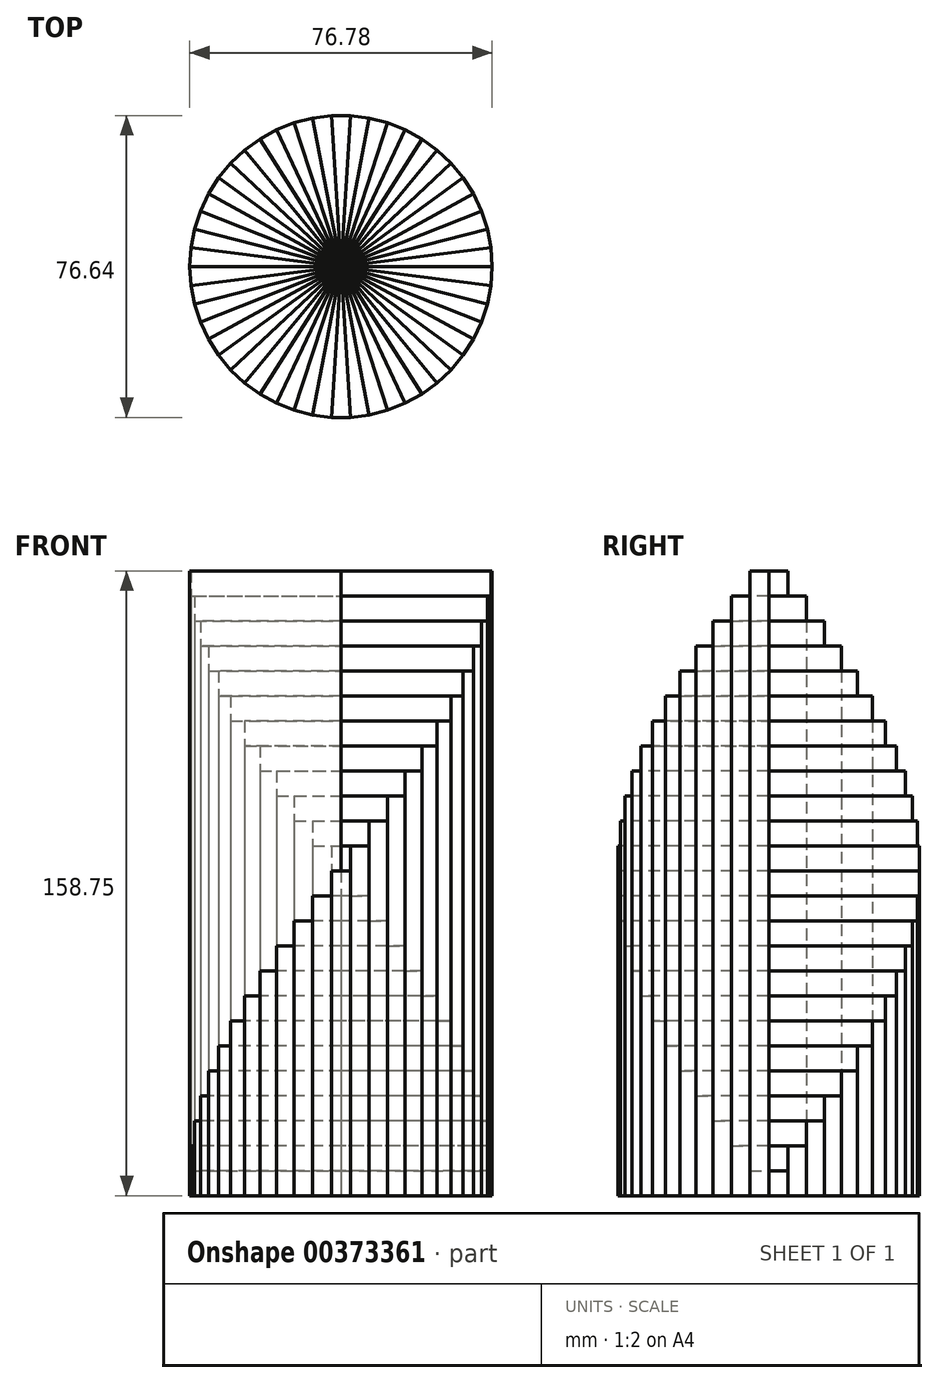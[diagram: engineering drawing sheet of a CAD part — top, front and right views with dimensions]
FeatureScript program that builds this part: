
annotation { "Feature Type Name" : "Feature", "Feature Type Description" : "" }
export const myFeature = defineFeature(function(context is Context, id is Id, definition is map)
    precondition{}
    {
        {
            var Q0;
            Q0=qCreatedBy(makeId("Top.planeOp"),FACE);
            var sketch = newSketch(context, id + "F0", { "sketchPlane" : qUnion([Q0])});
            skCircle(sketch, "E0.cCircle", {"center": v(0, 0) * mm, "radius": 38.32 * mm, "construction": true});
            skLineSegment(sketch, "E0.0", {"start": v(-2.41, 38.32) * mm, "end": v(2.41, 38.32) * mm});
            skLineSegment(sketch, "E0.1", {"start": v(2.41, 38.32) * mm, "end": v(7.2, 37.71) * mm});
            skLineSegment(sketch, "E0.2", {"start": v(7.2, 37.71) * mm, "end": v(11.86, 36.52) * mm});
            skLineSegment(sketch, "E0.3", {"start": v(11.86, 36.52) * mm, "end": v(16.35, 34.74) * mm});
            skLineSegment(sketch, "E0.4", {"start": v(16.35, 34.74) * mm, "end": v(20.57, 32.42) * mm});
            skLineSegment(sketch, "E0.5", {"start": v(20.57, 32.42) * mm, "end": v(24.47, 29.58) * mm});
            skLineSegment(sketch, "E0.6", {"start": v(24.47, 29.58) * mm, "end": v(27.99, 26.28) * mm});
            skLineSegment(sketch, "E0.7", {"start": v(27.99, 26.28) * mm, "end": v(31.06, 22.57) * mm});
            skLineSegment(sketch, "E0.8", {"start": v(31.06, 22.57) * mm, "end": v(33.65, 18.5) * mm});
            skLineSegment(sketch, "E0.9", {"start": v(33.65, 18.5) * mm, "end": v(35.7, 14.13) * mm});
            skLineSegment(sketch, "E0.10", {"start": v(35.7, 14.13) * mm, "end": v(37.19, 9.55) * mm});
            skLineSegment(sketch, "E0.11", {"start": v(37.19, 9.55) * mm, "end": v(38.1, 4.81) * mm});
            skLineSegment(sketch, "E0.12", {"start": v(38.1, 4.81) * mm, "end": v(38.4, 0) * mm});
            skLineSegment(sketch, "E0.13", {"start": v(38.4, 0) * mm, "end": v(38.1, -4.81) * mm});
            skLineSegment(sketch, "E0.14", {"start": v(38.1, -4.81) * mm, "end": v(37.19, -9.55) * mm});
            skLineSegment(sketch, "E0.15", {"start": v(37.19, -9.55) * mm, "end": v(35.7, -14.13) * mm});
            skLineSegment(sketch, "E0.16", {"start": v(35.7, -14.13) * mm, "end": v(33.65, -18.5) * mm});
            skLineSegment(sketch, "E0.17", {"start": v(33.65, -18.5) * mm, "end": v(31.06, -22.57) * mm});
            skLineSegment(sketch, "E0.18", {"start": v(31.06, -22.57) * mm, "end": v(27.99, -26.28) * mm});
            skLineSegment(sketch, "E0.19", {"start": v(27.99, -26.28) * mm, "end": v(24.47, -29.58) * mm});
            skLineSegment(sketch, "E0.20", {"start": v(24.47, -29.58) * mm, "end": v(20.57, -32.42) * mm});
            skLineSegment(sketch, "E0.21", {"start": v(20.57, -32.42) * mm, "end": v(16.35, -34.74) * mm});
            skLineSegment(sketch, "E0.22", {"start": v(16.35, -34.74) * mm, "end": v(11.86, -36.52) * mm});
            skLineSegment(sketch, "E0.23", {"start": v(11.86, -36.52) * mm, "end": v(7.2, -37.71) * mm});
            skLineSegment(sketch, "E0.24", {"start": v(7.2, -37.71) * mm, "end": v(2.41, -38.32) * mm});
            skLineSegment(sketch, "E0.25", {"start": v(2.41, -38.32) * mm, "end": v(-2.41, -38.32) * mm});
            skLineSegment(sketch, "E0.26", {"start": v(-2.41, -38.32) * mm, "end": v(-7.2, -37.71) * mm});
            skLineSegment(sketch, "E0.27", {"start": v(-7.2, -37.71) * mm, "end": v(-11.86, -36.52) * mm});
            skLineSegment(sketch, "E0.28", {"start": v(-11.86, -36.52) * mm, "end": v(-16.35, -34.74) * mm});
            skLineSegment(sketch, "E0.29", {"start": v(-16.35, -34.74) * mm, "end": v(-20.57, -32.42) * mm});
            skLineSegment(sketch, "E0.30", {"start": v(-20.57, -32.42) * mm, "end": v(-24.47, -29.58) * mm});
            skLineSegment(sketch, "E0.31", {"start": v(-24.47, -29.58) * mm, "end": v(-27.99, -26.28) * mm});
            skLineSegment(sketch, "E0.32", {"start": v(-27.99, -26.28) * mm, "end": v(-31.06, -22.57) * mm});
            skLineSegment(sketch, "E0.33", {"start": v(-31.06, -22.57) * mm, "end": v(-33.65, -18.5) * mm});
            skLineSegment(sketch, "E0.34", {"start": v(-33.65, -18.5) * mm, "end": v(-35.7, -14.13) * mm});
            skLineSegment(sketch, "E0.35", {"start": v(-35.7, -14.13) * mm, "end": v(-37.19, -9.55) * mm});
            skLineSegment(sketch, "E0.36", {"start": v(-37.19, -9.55) * mm, "end": v(-38.1, -4.81) * mm});
            skLineSegment(sketch, "E0.37", {"start": v(-38.1, -4.81) * mm, "end": v(-38.4, 0) * mm});
            skLineSegment(sketch, "E0.38", {"start": v(-38.4, 0) * mm, "end": v(-38.1, 4.81) * mm});
            skLineSegment(sketch, "E0.39", {"start": v(-38.1, 4.81) * mm, "end": v(-37.19, 9.55) * mm});
            skLineSegment(sketch, "E0.40", {"start": v(-37.19, 9.55) * mm, "end": v(-35.7, 14.13) * mm});
            skLineSegment(sketch, "E0.41", {"start": v(-35.7, 14.13) * mm, "end": v(-33.65, 18.5) * mm});
            skLineSegment(sketch, "E0.42", {"start": v(-33.65, 18.5) * mm, "end": v(-31.06, 22.57) * mm});
            skLineSegment(sketch, "E0.43", {"start": v(-31.06, 22.57) * mm, "end": v(-27.99, 26.28) * mm});
            skLineSegment(sketch, "E0.44", {"start": v(-27.99, 26.28) * mm, "end": v(-24.47, 29.58) * mm});
            skLineSegment(sketch, "E0.45", {"start": v(-24.47, 29.58) * mm, "end": v(-20.57, 32.42) * mm});
            skLineSegment(sketch, "E0.46", {"start": v(-20.57, 32.42) * mm, "end": v(-16.35, 34.74) * mm});
            skLineSegment(sketch, "E0.47", {"start": v(-16.35, 34.74) * mm, "end": v(-11.86, 36.52) * mm});
            skLineSegment(sketch, "E0.48", {"start": v(-11.86, 36.52) * mm, "end": v(-7.2, 37.71) * mm});
            skLineSegment(sketch, "E0.49", {"start": v(-7.2, 37.71) * mm, "end": v(-2.41, 38.32) * mm});
            skPoint(sketch, "E0.0.midPoint", {"position": v(0, 38.32) * mm});
            skLineSegment(sketch, "E1", {"start": v(-38.4, 0) * mm, "end": v(38.4, 0) * mm});
            skLineSegment(sketch, "E2", {"start": v(38.1, 4.81) * mm, "end": v(-38.1, -4.81) * mm});
            skLineSegment(sketch, "E3", {"start": v(37.19, 9.55) * mm, "end": v(-37.19, -9.55) * mm});
            skLineSegment(sketch, "E4", {"start": v(35.7, 14.13) * mm, "end": v(-35.7, -14.13) * mm});
            skLineSegment(sketch, "E5", {"start": v(33.65, 18.5) * mm, "end": v(-33.65, -18.5) * mm});
            skLineSegment(sketch, "E6", {"start": v(31.06, 22.57) * mm, "end": v(-31.06, -22.57) * mm});
            skLineSegment(sketch, "E7", {"start": v(27.99, 26.28) * mm, "end": v(-27.99, -26.28) * mm});
            skLineSegment(sketch, "E8", {"start": v(24.47, 29.58) * mm, "end": v(-24.47, -29.58) * mm});
            skLineSegment(sketch, "E9", {"start": v(20.57, 32.42) * mm, "end": v(-20.57, -32.42) * mm});
            skLineSegment(sketch, "E10", {"start": v(16.35, 34.74) * mm, "end": v(-16.35, -34.74) * mm});
            skLineSegment(sketch, "E11", {"start": v(11.86, 36.52) * mm, "end": v(-11.86, -36.52) * mm});
            skLineSegment(sketch, "E12", {"start": v(7.2, 37.71) * mm, "end": v(-7.2, -37.71) * mm});
            skLineSegment(sketch, "E13", {"start": v(2.41, 38.32) * mm, "end": v(-2.41, -38.32) * mm});
            skLineSegment(sketch, "E14", {"start": v(-2.41, 38.32) * mm, "end": v(2.41, -38.32) * mm});
            skLineSegment(sketch, "E15", {"start": v(-7.2, 37.71) * mm, "end": v(7.2, -37.71) * mm});
            skLineSegment(sketch, "E16", {"start": v(-11.86, 36.52) * mm, "end": v(11.86, -36.52) * mm});
            skLineSegment(sketch, "E17", {"start": v(-16.35, 34.74) * mm, "end": v(16.35, -34.74) * mm});
            skLineSegment(sketch, "E18", {"start": v(-20.57, 32.42) * mm, "end": v(20.57, -32.42) * mm});
            skLineSegment(sketch, "E19", {"start": v(24.47, -29.58) * mm, "end": v(-24.47, 29.58) * mm});
            skLineSegment(sketch, "E20", {"start": v(-27.99, 26.28) * mm, "end": v(27.99, -26.28) * mm});
            skLineSegment(sketch, "E21", {"start": v(31.06, -22.57) * mm, "end": v(-31.06, 22.57) * mm});
            skLineSegment(sketch, "E22", {"start": v(-33.65, 18.5) * mm, "end": v(33.65, -18.5) * mm});
            skLineSegment(sketch, "E23", {"start": v(35.7, -14.13) * mm, "end": v(-35.7, 14.13) * mm});
            skLineSegment(sketch, "E24", {"start": v(-37.19, 9.55) * mm, "end": v(37.19, -9.55) * mm});
            skLineSegment(sketch, "E25", {"start": v(-38.1, 4.81) * mm, "end": v(38.1, -4.81) * mm});
            skSolve(sketch);
        }
        {
            var Q0;
            {var subQ0=sQuery(id+"F0.wireOp",EDGE,"E0.12");Q0=makeQuery(id+"F0.imprint","IMPRINT",FACE,{"disambiguationData":[TD([[makeQuery(id+"F0.imprint","IMPRINT",EDGE,{"derivedFrom":subQ0}),-1.0]])]});}
            var Q1;
            {var subQ0=sQuery(id+"F0.wireOp",EDGE,"E0.37");Q1=makeQuery(id+"F0.imprint","IMPRINT",FACE,{"disambiguationData":[TD([[makeQuery(id+"F0.imprint","IMPRINT",EDGE,{"derivedFrom":subQ0}),-1.0]])]});}
            extrude(context, id + "F1", {"entities" : qUnion([Q0, Q1]), "depth" : 6.35 * mm});
        }
        {
            var Q0;
            {var subQ0=sQuery(id+"F0.wireOp",EDGE,"E0.11");Q0=makeQuery(id+"F0.imprint","IMPRINT",FACE,{"disambiguationData":[TD([[makeQuery(id+"F0.imprint","IMPRINT",EDGE,{"derivedFrom":subQ0}),-1.0]])]});}
            var Q1;
            {var subQ0=sQuery(id+"F0.wireOp",EDGE,"E0.36");Q1=makeQuery(id+"F0.imprint","IMPRINT",FACE,{"disambiguationData":[TD([[makeQuery(id+"F0.imprint","IMPRINT",EDGE,{"derivedFrom":subQ0}),-1.0]])]});}
            extrude(context, id + "F2", {"entities" : qUnion([Q0, Q1]), "depth" : 12.7 * mm});
        }
        {
            var Q0;
            {var subQ0=sQuery(id+"F0.wireOp",EDGE,"E0.10");Q0=makeQuery(id+"F0.imprint","IMPRINT",FACE,{"disambiguationData":[TD([[makeQuery(id+"F0.imprint","IMPRINT",EDGE,{"derivedFrom":subQ0}),-1.0]])]});}
            var Q1;
            {var subQ0=sQuery(id+"F0.wireOp",EDGE,"E0.35");Q1=makeQuery(id+"F0.imprint","IMPRINT",FACE,{"disambiguationData":[TD([[makeQuery(id+"F0.imprint","IMPRINT",EDGE,{"derivedFrom":subQ0}),-1.0]])]});}
            extrude(context, id + "F3", {"entities" : qUnion([Q0, Q1]), "depth" : 19.05 * mm});
        }
        {
            var Q0;
            {var subQ0=sQuery(id+"F0.wireOp",EDGE,"E0.9");Q0=makeQuery(id+"F0.imprint","IMPRINT",FACE,{"disambiguationData":[TD([[makeQuery(id+"F0.imprint","IMPRINT",EDGE,{"derivedFrom":subQ0}),-1.0]])]});}
            var Q1;
            {var subQ0=sQuery(id+"F0.wireOp",EDGE,"E0.34");Q1=makeQuery(id+"F0.imprint","IMPRINT",FACE,{"disambiguationData":[TD([[makeQuery(id+"F0.imprint","IMPRINT",EDGE,{"derivedFrom":subQ0}),-1.0]])]});}
            extrude(context, id + "F4", {"entities" : qUnion([Q0, Q1]), "depth" : 25.4 * mm});
        }
        {
            var Q0;
            {var subQ0=sQuery(id+"F0.wireOp",EDGE,"E0.8");Q0=makeQuery(id+"F0.imprint","IMPRINT",FACE,{"disambiguationData":[TD([[makeQuery(id+"F0.imprint","IMPRINT",EDGE,{"derivedFrom":subQ0}),-1.0]])]});}
            var Q1;
            {var subQ0=sQuery(id+"F0.wireOp",EDGE,"E0.33");Q1=makeQuery(id+"F0.imprint","IMPRINT",FACE,{"disambiguationData":[TD([[makeQuery(id+"F0.imprint","IMPRINT",EDGE,{"derivedFrom":subQ0}),-1.0]])]});}
            extrude(context, id + "F5", {"entities" : qUnion([Q0, Q1]), "depth" : 31.75 * mm});
        }
        {
            var Q0;
            {var subQ0=sQuery(id+"F0.wireOp",EDGE,"E0.7");Q0=makeQuery(id+"F0.imprint","IMPRINT",FACE,{"disambiguationData":[TD([[makeQuery(id+"F0.imprint","IMPRINT",EDGE,{"derivedFrom":subQ0}),-1.0]])]});}
            var Q1;
            {var subQ0=sQuery(id+"F0.wireOp",EDGE,"E0.32");Q1=makeQuery(id+"F0.imprint","IMPRINT",FACE,{"disambiguationData":[TD([[makeQuery(id+"F0.imprint","IMPRINT",EDGE,{"derivedFrom":subQ0}),-1.0]])]});}
            extrude(context, id + "F6", {"entities" : qUnion([Q0, Q1]), "depth" : 38.1 * mm});
        }
        {
            var Q0;
            {var subQ0=sQuery(id+"F0.wireOp",EDGE,"E0.6");Q0=makeQuery(id+"F0.imprint","IMPRINT",FACE,{"disambiguationData":[TD([[makeQuery(id+"F0.imprint","IMPRINT",EDGE,{"derivedFrom":subQ0}),-1.0]])]});}
            var Q1;
            {var subQ0=sQuery(id+"F0.wireOp",EDGE,"E0.31");Q1=makeQuery(id+"F0.imprint","IMPRINT",FACE,{"disambiguationData":[TD([[makeQuery(id+"F0.imprint","IMPRINT",EDGE,{"derivedFrom":subQ0}),-1.0]])]});}
            extrude(context, id + "F7", {"entities" : qUnion([Q0, Q1]), "depth" : 44.45 * mm});
        }
        {
            var Q0;
            {var subQ0=sQuery(id+"F0.wireOp",EDGE,"E0.5");Q0=makeQuery(id+"F0.imprint","IMPRINT",FACE,{"disambiguationData":[TD([[makeQuery(id+"F0.imprint","IMPRINT",EDGE,{"derivedFrom":subQ0}),-1.0]])]});}
            var Q1;
            {var subQ0=sQuery(id+"F0.wireOp",EDGE,"E0.30");Q1=makeQuery(id+"F0.imprint","IMPRINT",FACE,{"disambiguationData":[TD([[makeQuery(id+"F0.imprint","IMPRINT",EDGE,{"derivedFrom":subQ0}),-1.0]])]});}
            extrude(context, id + "F8", {"entities" : qUnion([Q0, Q1]), "depth" : 50.8 * mm});
        }
        {
            var Q0;
            {var subQ0=sQuery(id+"F0.wireOp",EDGE,"E0.4");Q0=makeQuery(id+"F0.imprint","IMPRINT",FACE,{"disambiguationData":[TD([[makeQuery(id+"F0.imprint","IMPRINT",EDGE,{"derivedFrom":subQ0}),-1.0]])]});}
            var Q1;
            {var subQ0=sQuery(id+"F0.wireOp",EDGE,"E0.29");Q1=makeQuery(id+"F0.imprint","IMPRINT",FACE,{"disambiguationData":[TD([[makeQuery(id+"F0.imprint","IMPRINT",EDGE,{"derivedFrom":subQ0}),-1.0]])]});}
            extrude(context, id + "F9", {"entities" : qUnion([Q0, Q1]), "depth" : 57.15 * mm});
        }
        {
            var Q0;
            {var subQ0=sQuery(id+"F0.wireOp",EDGE,"E0.3");Q0=makeQuery(id+"F0.imprint","IMPRINT",FACE,{"disambiguationData":[TD([[makeQuery(id+"F0.imprint","IMPRINT",EDGE,{"derivedFrom":subQ0}),-1.0]])]});}
            var Q1;
            {var subQ0=sQuery(id+"F0.wireOp",EDGE,"E0.28");Q1=makeQuery(id+"F0.imprint","IMPRINT",FACE,{"disambiguationData":[TD([[makeQuery(id+"F0.imprint","IMPRINT",EDGE,{"derivedFrom":subQ0}),-1.0]])]});}
            extrude(context, id + "F10", {"entities" : qUnion([Q0, Q1]), "depth" : 63.5 * mm});
        }
        {
            var Q0;
            {var subQ0=sQuery(id+"F0.wireOp",EDGE,"E0.2");Q0=makeQuery(id+"F0.imprint","IMPRINT",FACE,{"disambiguationData":[TD([[makeQuery(id+"F0.imprint","IMPRINT",EDGE,{"derivedFrom":subQ0}),-1.0]])]});}
            var Q1;
            {var subQ0=sQuery(id+"F0.wireOp",EDGE,"E0.27");Q1=makeQuery(id+"F0.imprint","IMPRINT",FACE,{"disambiguationData":[TD([[makeQuery(id+"F0.imprint","IMPRINT",EDGE,{"derivedFrom":subQ0}),-1.0]])]});}
            extrude(context, id + "F11", {"entities" : qUnion([Q0, Q1]), "depth" : 69.85 * mm});
        }
        {
            var Q0;
            {var subQ0=sQuery(id+"F0.wireOp",EDGE,"E0.1");Q0=makeQuery(id+"F0.imprint","IMPRINT",FACE,{"disambiguationData":[TD([[makeQuery(id+"F0.imprint","IMPRINT",EDGE,{"derivedFrom":subQ0}),-1.0]])]});}
            var Q1;
            {var subQ0=sQuery(id+"F0.wireOp",EDGE,"E0.26");Q1=makeQuery(id+"F0.imprint","IMPRINT",FACE,{"disambiguationData":[TD([[makeQuery(id+"F0.imprint","IMPRINT",EDGE,{"derivedFrom":subQ0}),-1.0]])]});}
            extrude(context, id + "F12", {"entities" : qUnion([Q0, Q1]), "depth" : 76.2 * mm});
        }
        {
            var Q0;
            {var subQ0=sQuery(id+"F0.wireOp",EDGE,"E0.0");Q0=makeQuery(id+"F0.imprint","IMPRINT",FACE,{"disambiguationData":[TD([[makeQuery(id+"F0.imprint","IMPRINT",EDGE,{"derivedFrom":subQ0}),-1.0]])]});}
            var Q1;
            {var subQ0=sQuery(id+"F0.wireOp",EDGE,"E0.25");Q1=makeQuery(id+"F0.imprint","IMPRINT",FACE,{"disambiguationData":[TD([[makeQuery(id+"F0.imprint","IMPRINT",EDGE,{"derivedFrom":subQ0}),-1.0]])]});}
            extrude(context, id + "F13", {"entities" : qUnion([Q0, Q1]), "depth" : 82.55 * mm});
        }
        {
            var Q0;
            {var subQ0=sQuery(id+"F0.wireOp",EDGE,"E0.49");Q0=makeQuery(id+"F0.imprint","IMPRINT",FACE,{"disambiguationData":[TD([[makeQuery(id+"F0.imprint","IMPRINT",EDGE,{"derivedFrom":subQ0}),-1.0]])]});}
            var Q1;
            {var subQ0=sQuery(id+"F0.wireOp",EDGE,"E0.24");Q1=makeQuery(id+"F0.imprint","IMPRINT",FACE,{"disambiguationData":[TD([[makeQuery(id+"F0.imprint","IMPRINT",EDGE,{"derivedFrom":subQ0}),-1.0]])]});}
            extrude(context, id + "F14", {"entities" : qUnion([Q0, Q1]), "depth" : 88.9 * mm});
        }
        {
            var Q0;
            {var subQ0=sQuery(id+"F0.wireOp",EDGE,"E0.48");Q0=makeQuery(id+"F0.imprint","IMPRINT",FACE,{"disambiguationData":[TD([[makeQuery(id+"F0.imprint","IMPRINT",EDGE,{"derivedFrom":subQ0}),-1.0]])]});}
            var Q1;
            {var subQ0=sQuery(id+"F0.wireOp",EDGE,"E0.23");Q1=makeQuery(id+"F0.imprint","IMPRINT",FACE,{"disambiguationData":[TD([[makeQuery(id+"F0.imprint","IMPRINT",EDGE,{"derivedFrom":subQ0}),-1.0]])]});}
            extrude(context, id + "F15", {"entities" : qUnion([Q0, Q1]), "depth" : 95.25 * mm});
        }
        {
            var Q0;
            {var subQ0=sQuery(id+"F0.wireOp",EDGE,"E0.47");Q0=makeQuery(id+"F0.imprint","IMPRINT",FACE,{"disambiguationData":[TD([[makeQuery(id+"F0.imprint","IMPRINT",EDGE,{"derivedFrom":subQ0}),-1.0]])]});}
            var Q1;
            {var subQ0=sQuery(id+"F0.wireOp",EDGE,"E0.22");Q1=makeQuery(id+"F0.imprint","IMPRINT",FACE,{"disambiguationData":[TD([[makeQuery(id+"F0.imprint","IMPRINT",EDGE,{"derivedFrom":subQ0}),-1.0]])]});}
            extrude(context, id + "F16", {"entities" : qUnion([Q0, Q1]), "depth" : 101.6 * mm});
        }
        {
            var Q0;
            {var subQ0=sQuery(id+"F0.wireOp",EDGE,"E0.46");Q0=makeQuery(id+"F0.imprint","IMPRINT",FACE,{"disambiguationData":[TD([[makeQuery(id+"F0.imprint","IMPRINT",EDGE,{"derivedFrom":subQ0}),-1.0]])]});}
            var Q1;
            {var subQ0=sQuery(id+"F0.wireOp",EDGE,"E0.21");Q1=makeQuery(id+"F0.imprint","IMPRINT",FACE,{"disambiguationData":[TD([[makeQuery(id+"F0.imprint","IMPRINT",EDGE,{"derivedFrom":subQ0}),-1.0]])]});}
            extrude(context, id + "F17", {"entities" : qUnion([Q0, Q1]), "depth" : 107.95 * mm});
        }
        {
            var Q0;
            {var subQ0=sQuery(id+"F0.wireOp",EDGE,"E0.45");Q0=makeQuery(id+"F0.imprint","IMPRINT",FACE,{"disambiguationData":[TD([[makeQuery(id+"F0.imprint","IMPRINT",EDGE,{"derivedFrom":subQ0}),-1.0]])]});}
            var Q1;
            {var subQ0=sQuery(id+"F0.wireOp",EDGE,"E0.20");Q1=makeQuery(id+"F0.imprint","IMPRINT",FACE,{"disambiguationData":[TD([[makeQuery(id+"F0.imprint","IMPRINT",EDGE,{"derivedFrom":subQ0}),-1.0]])]});}
            extrude(context, id + "F18", {"entities" : qUnion([Q0, Q1]), "depth" : 114.3 * mm});
        }
        {
            var Q0;
            {var subQ0=sQuery(id+"F0.wireOp",EDGE,"E0.44");Q0=makeQuery(id+"F0.imprint","IMPRINT",FACE,{"disambiguationData":[TD([[makeQuery(id+"F0.imprint","IMPRINT",EDGE,{"derivedFrom":subQ0}),-1.0]])]});}
            var Q1;
            {var subQ0=sQuery(id+"F0.wireOp",EDGE,"E0.19");Q1=makeQuery(id+"F0.imprint","IMPRINT",FACE,{"disambiguationData":[TD([[makeQuery(id+"F0.imprint","IMPRINT",EDGE,{"derivedFrom":subQ0}),-1.0]])]});}
            extrude(context, id + "F19", {"entities" : qUnion([Q0, Q1]), "depth" : 120.65 * mm});
        }
        {
            var Q0;
            {var subQ0=sQuery(id+"F0.wireOp",EDGE,"E0.43");Q0=makeQuery(id+"F0.imprint","IMPRINT",FACE,{"disambiguationData":[TD([[makeQuery(id+"F0.imprint","IMPRINT",EDGE,{"derivedFrom":subQ0}),-1.0]])]});}
            var Q1;
            {var subQ0=sQuery(id+"F0.wireOp",EDGE,"E0.18");Q1=makeQuery(id+"F0.imprint","IMPRINT",FACE,{"disambiguationData":[TD([[makeQuery(id+"F0.imprint","IMPRINT",EDGE,{"derivedFrom":subQ0}),-1.0]])]});}
            extrude(context, id + "F20", {"entities" : qUnion([Q0, Q1]), "depth" : 127 * mm});
        }
        {
            var Q0;
            {var subQ0=sQuery(id+"F0.wireOp",EDGE,"E0.42");Q0=makeQuery(id+"F0.imprint","IMPRINT",FACE,{"disambiguationData":[TD([[makeQuery(id+"F0.imprint","IMPRINT",EDGE,{"derivedFrom":subQ0}),-1.0]])]});}
            var Q1;
            {var subQ0=sQuery(id+"F0.wireOp",EDGE,"E0.17");Q1=makeQuery(id+"F0.imprint","IMPRINT",FACE,{"disambiguationData":[TD([[makeQuery(id+"F0.imprint","IMPRINT",EDGE,{"derivedFrom":subQ0}),-1.0]])]});}
            extrude(context, id + "F21", {"entities" : qUnion([Q0, Q1]), "depth" : 133.35 * mm});
        }
        {
            var Q0;
            {var subQ0=sQuery(id+"F0.wireOp",EDGE,"E0.41");Q0=makeQuery(id+"F0.imprint","IMPRINT",FACE,{"disambiguationData":[TD([[makeQuery(id+"F0.imprint","IMPRINT",EDGE,{"derivedFrom":subQ0}),-1.0]])]});}
            var Q1;
            {var subQ0=sQuery(id+"F0.wireOp",EDGE,"E0.16");Q1=makeQuery(id+"F0.imprint","IMPRINT",FACE,{"disambiguationData":[TD([[makeQuery(id+"F0.imprint","IMPRINT",EDGE,{"derivedFrom":subQ0}),-1.0]])]});}
            extrude(context, id + "F22", {"entities" : qUnion([Q0, Q1]), "depth" : 139.7 * mm});
        }
        {
            var Q0;
            {var subQ0=sQuery(id+"F0.wireOp",EDGE,"E0.40");Q0=makeQuery(id+"F0.imprint","IMPRINT",FACE,{"disambiguationData":[TD([[makeQuery(id+"F0.imprint","IMPRINT",EDGE,{"derivedFrom":subQ0}),-1.0]])]});}
            var Q1;
            {var subQ0=sQuery(id+"F0.wireOp",EDGE,"E0.15");Q1=makeQuery(id+"F0.imprint","IMPRINT",FACE,{"disambiguationData":[TD([[makeQuery(id+"F0.imprint","IMPRINT",EDGE,{"derivedFrom":subQ0}),-1.0]])]});}
            extrude(context, id + "F23", {"entities" : qUnion([Q0, Q1]), "depth" : 146.05 * mm});
        }
        {
            var Q0;
            {var subQ0=sQuery(id+"F0.wireOp",EDGE,"E0.39");Q0=makeQuery(id+"F0.imprint","IMPRINT",FACE,{"disambiguationData":[TD([[makeQuery(id+"F0.imprint","IMPRINT",EDGE,{"derivedFrom":subQ0}),-1.0]])]});}
            var Q1;
            {var subQ0=sQuery(id+"F0.wireOp",EDGE,"E0.14");Q1=makeQuery(id+"F0.imprint","IMPRINT",FACE,{"disambiguationData":[TD([[makeQuery(id+"F0.imprint","IMPRINT",EDGE,{"derivedFrom":subQ0}),-1.0]])]});}
            extrude(context, id + "F24", {"entities" : qUnion([Q0, Q1]), "depth" : 152.4 * mm});
        }
        {
            var Q0;
            {var subQ0=sQuery(id+"F0.wireOp",EDGE,"E0.38");Q0=makeQuery(id+"F0.imprint","IMPRINT",FACE,{"disambiguationData":[TD([[makeQuery(id+"F0.imprint","IMPRINT",EDGE,{"derivedFrom":subQ0}),-1.0]])]});}
            var Q1;
            {var subQ0=sQuery(id+"F0.wireOp",EDGE,"E0.13");Q1=makeQuery(id+"F0.imprint","IMPRINT",FACE,{"disambiguationData":[TD([[makeQuery(id+"F0.imprint","IMPRINT",EDGE,{"derivedFrom":subQ0}),-1.0]])]});}
            extrude(context, id + "F25", {"entities" : qUnion([Q0, Q1]), "depth" : 158.75 * mm});
        }
    });
